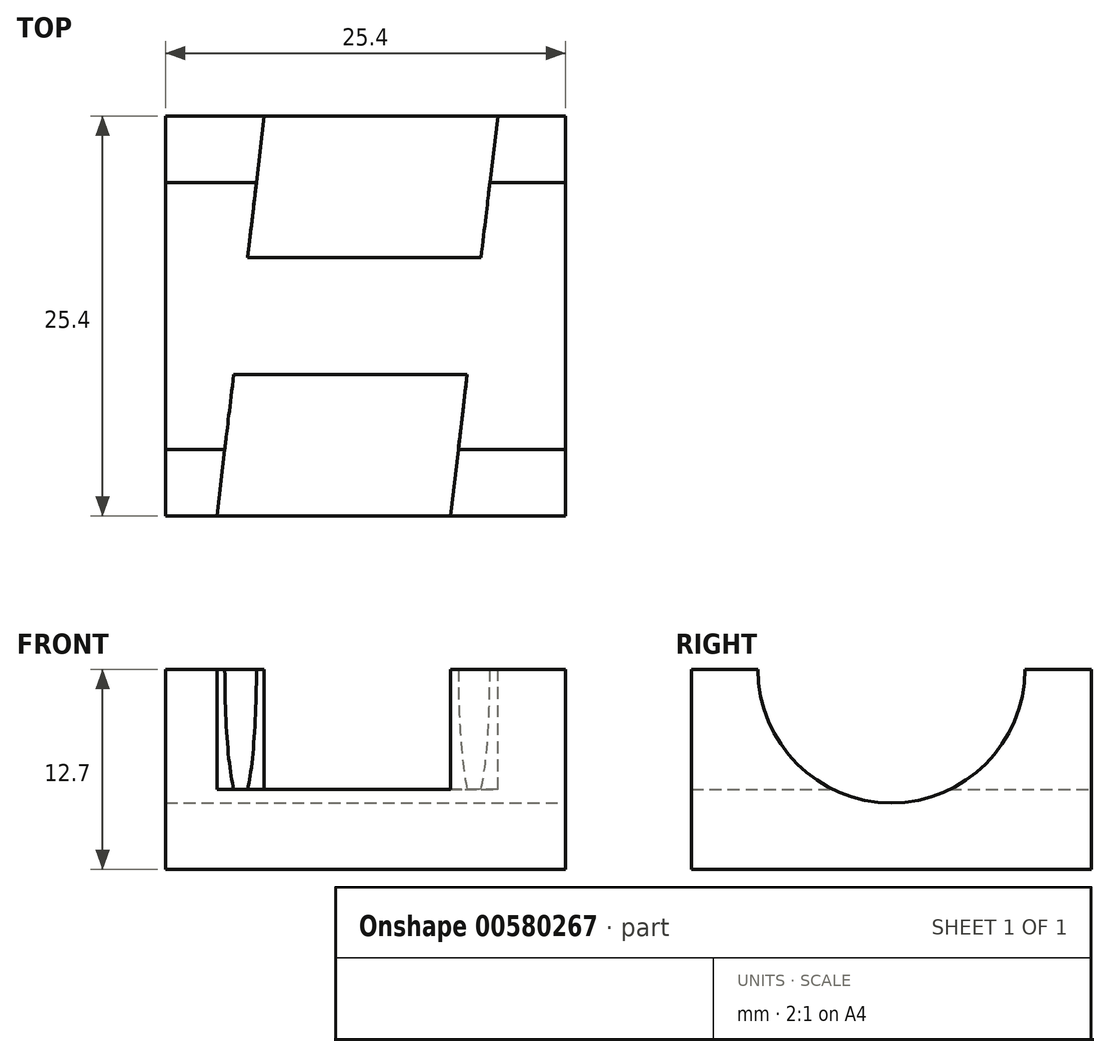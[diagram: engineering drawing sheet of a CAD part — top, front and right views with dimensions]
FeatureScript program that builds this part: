
annotation { "Feature Type Name" : "Feature", "Feature Type Description" : "" }
export const myFeature = defineFeature(function(context is Context, id is Id, definition is map)
    precondition{}
    {
        {
            var Q0;
            Q0=qCreatedBy(makeId("Front.planeOp"),FACE);
            var sketch = newSketch(context, id + "F0", { "sketchPlane" : qUnion([Q0])});
            skLineSegment(sketch, "E0.bottom", {"start": v(12.7, 6.35) * mm, "end": v(-12.7, 6.35) * mm});
            skLineSegment(sketch, "E0.top", {"start": v(12.7, -6.35) * mm, "end": v(-12.7, -6.35) * mm});
            skLineSegment(sketch, "E0.left", {"start": v(12.7, 6.35) * mm, "end": v(12.7, -6.35) * mm});
            skLineSegment(sketch, "E0.right", {"start": v(-12.7, 6.35) * mm, "end": v(-12.7, -6.35) * mm});
            skPoint(sketch, "E0.middle", {"position": v(0, 0) * mm});
            skSolve(sketch);
        }
        {
            var Q0;
            Q0 = qSketchRegion(id + "F0", true);
            extrude(context, id + "F1", {"entities" : qUnion([Q0]), "depth" : 25.4 * mm, "offsetDistance" : 25.4 * mm});
        }
        {
            var Q0;
            Q0=makeQuery(id+"F1.opExtrude","SWEPT_FACE",FACE,{"disambiguationData":[OSD([sQuery(id+"F0.wireOp",EDGE,"E0.bottom")])]});
            var sketch = newSketch(context, id + "F2", { "sketchPlane" : qUnion([Q0])});
            skLineSegment(sketch, "E1", {"start": v(-9.44, -25.4) * mm, "end": v(-6.43, 0) * mm});
            skLineSegment(sketch, "E2", {"start": v(5.56, -25.4) * mm, "end": v(8.57, 0) * mm});
            skLineSegment(sketch, "E3", {"start": v(-1.92, -25.4) * mm, "end": v(1.09, 0) * mm});
            skSolve(sketch);
        }
        {
            var Q0;
            {var subQ0=sQuery(id+"F2.wireOp",EDGE,"E1");Q0=makeQuery(id+"F2.imprint","IMPRINT",FACE,{"disambiguationData":[TD([[makeQuery(id+"F2.imprint","IMPRINT",EDGE,{"derivedFrom":subQ0}),-1.0]])]});}
            extrude(context, id + "F3", {"entities" : qUnion([Q0]), "operationType" : NewBodyOperationType.REMOVE, "oppositeDirection" : true, "depth" : 7.62 * mm, "offsetDistance" : 25.4 * mm});
        }
        {
            var Q0;
            {var subQ1=sQuery(id+"F0.wireOp",EDGE,"E0.left");var subQ3=sQuery(id+"F0.wireOp",EDGE,"E0.bottom");Q0=makeQuery(id+"F3.boolean.opBoolean","SPLIT",FACE,{"disambiguationData":[TD([makeQuery(id+"F1.opExtrude","SWEPT_FACE",FACE,{"disambiguationData":[OSD([subQ1])]})])],"derivedFrom":makeQuery(id+"F1.opExtrude","SWEPT_FACE",FACE,{"disambiguationData":[OSD([subQ3])]})});}
            var sketch = newSketch(context, id + "F4", { "sketchPlane" : qUnion([Q0])});
            skLineSegment(sketch, "E4", {"start": v(5.4, -25.4) * mm, "end": v(8.4, 0) * mm});
            skSolve(sketch);
        }
        {
            var Q0;
            {var subQ0=sQuery(id+"F4.wireOp",EDGE,"E4");Q0=makeQuery(id+"F4.imprint","IMPRINT",FACE,{"disambiguationData":[TD([[makeQuery(id+"F4.imprint","IMPRINT",EDGE,{"derivedFrom":subQ0}),1.0]])]});}
            extrude(context, id + "F5", {"entities" : qUnion([Q0]), "operationType" : NewBodyOperationType.REMOVE, "oppositeDirection" : true, "depth" : 7.62 * mm, "offsetDistance" : 25.4 * mm});
        }
        {
            var Q0;
            Q0=makeQuery(id+"F1.opExtrude","SWEPT_FACE",FACE,{"disambiguationData":[OSD([sQuery(id+"F0.wireOp",EDGE,"E0.left")])]});
            var sketch = newSketch(context, id + "F6", { "sketchPlane" : qUnion([Q0])});
            skCircle(sketch, "E5", {"center": v(-12.7, 6.35) * mm, "radius": 8.48 * mm});
            skSolve(sketch);
        }
        {
            var Q0;
            Q0 = qSketchRegion(id + "F6", true);
            extrude(context, id + "F7", {"entities" : qUnion([Q0]), "operationType" : NewBodyOperationType.REMOVE, "oppositeDirection" : true, "depth" : 25.4 * mm, "offsetDistance" : 25.4 * mm});
        }
    });
